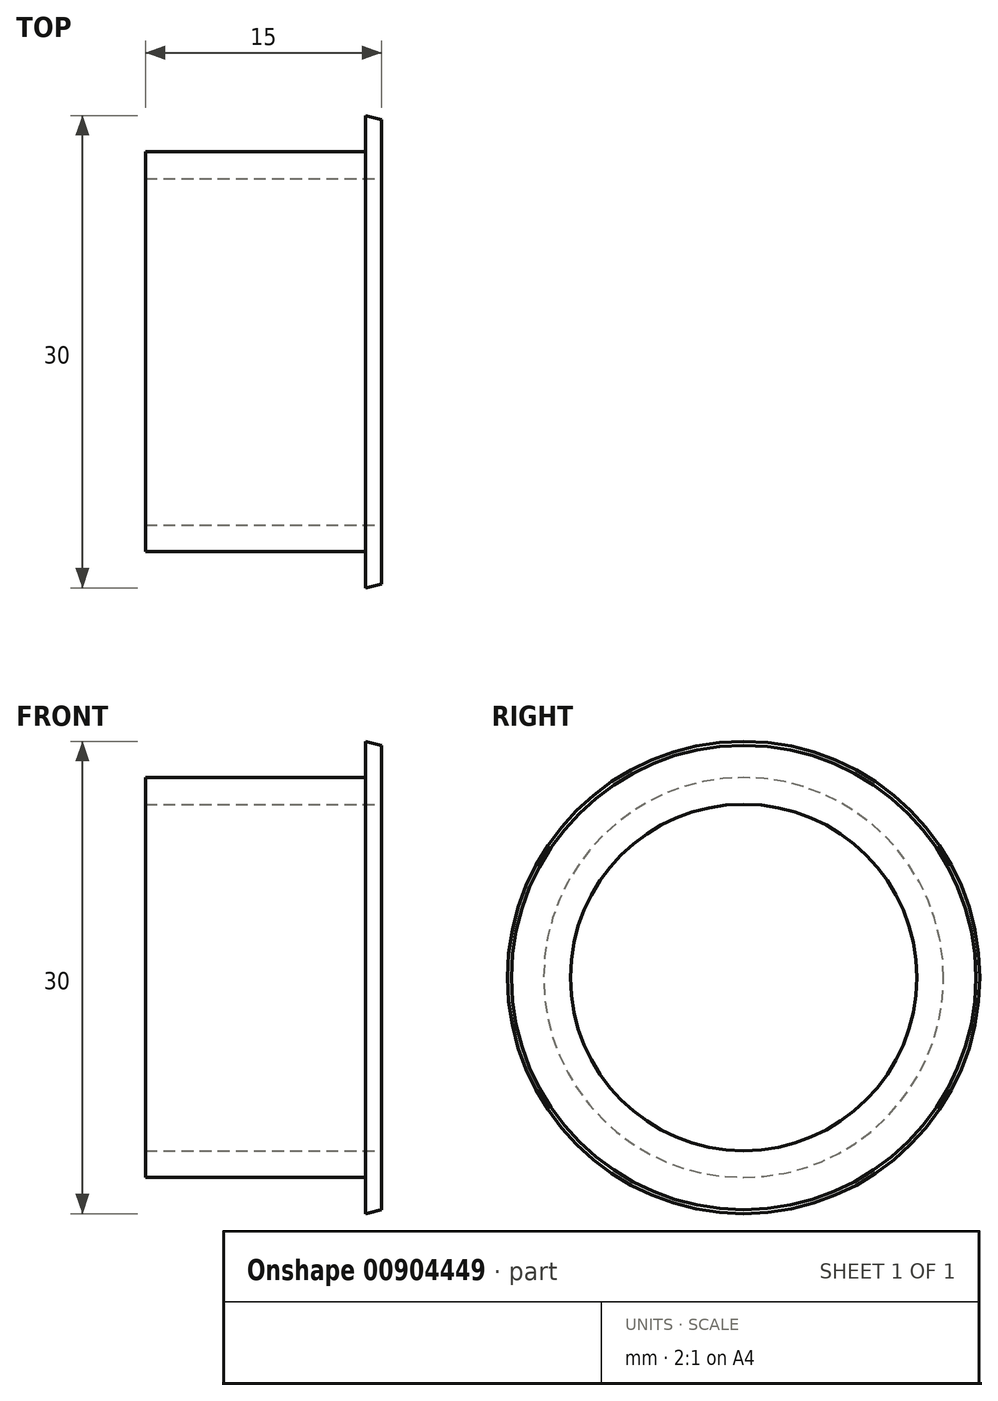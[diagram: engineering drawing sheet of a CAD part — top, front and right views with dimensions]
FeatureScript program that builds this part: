
annotation { "Feature Type Name" : "Feature", "Feature Type Description" : "" }
export const myFeature = defineFeature(function(context is Context, id is Id, definition is map)
    precondition{}
    {
        {
            var Q0;
            Q0=qCreatedBy(makeId("Front.planeOp"),FACE);
            var sketch = newSketch(context, id + "F0", { "sketchPlane" : qUnion([Q0])});
            skLineSegment(sketch, "E0", {"start": v(0, 0) * mm, "end": v(-15, 0) * mm, "construction": true});
            skLineSegment(sketch, "E1", {"start": v(-15, 11) * mm, "end": v(-15, 12.7) * mm});
            skLineSegment(sketch, "E2", {"start": v(-15, 12.7) * mm, "end": v(-1, 12.7) * mm});
            skLineSegment(sketch, "E3", {"start": v(0, 14.75) * mm, "end": v(0, 11) * mm});
            skLineSegment(sketch, "E4", {"start": v(-15, 11) * mm, "end": v(0, 11) * mm});
            skLineSegment(sketch, "E5", {"start": v(-1, 12.7) * mm, "end": v(-1, 15) * mm});
            skLineSegment(sketch, "E6", {"start": v(-1, 15) * mm, "end": v(0, 14.75) * mm});
            skSolve(sketch);
        }
        {
            var Q0;
            Q0=makeQuery(id+"F0.imprint","IMPRINT",FACE,{"disambiguationData":[TD([[makeQuery(id+"F0.imprint","IMPRINT",EDGE,{"derivedFrom":sQuery(id+"F0.wireOp",EDGE,"E1")}),-1.0]])]});
            var Q1;
            Q1=sQuery(id+"F0.wireOp",EDGE,"E0");
            revolve(context, id + "F1", {"surfaceOperationType" : NewSurfaceOperationType.NEW, "entities" : qUnion([Q0]), "axis" : qUnion([Q1]), "revolveType" : RevolveType.FULL});
        }
    });
